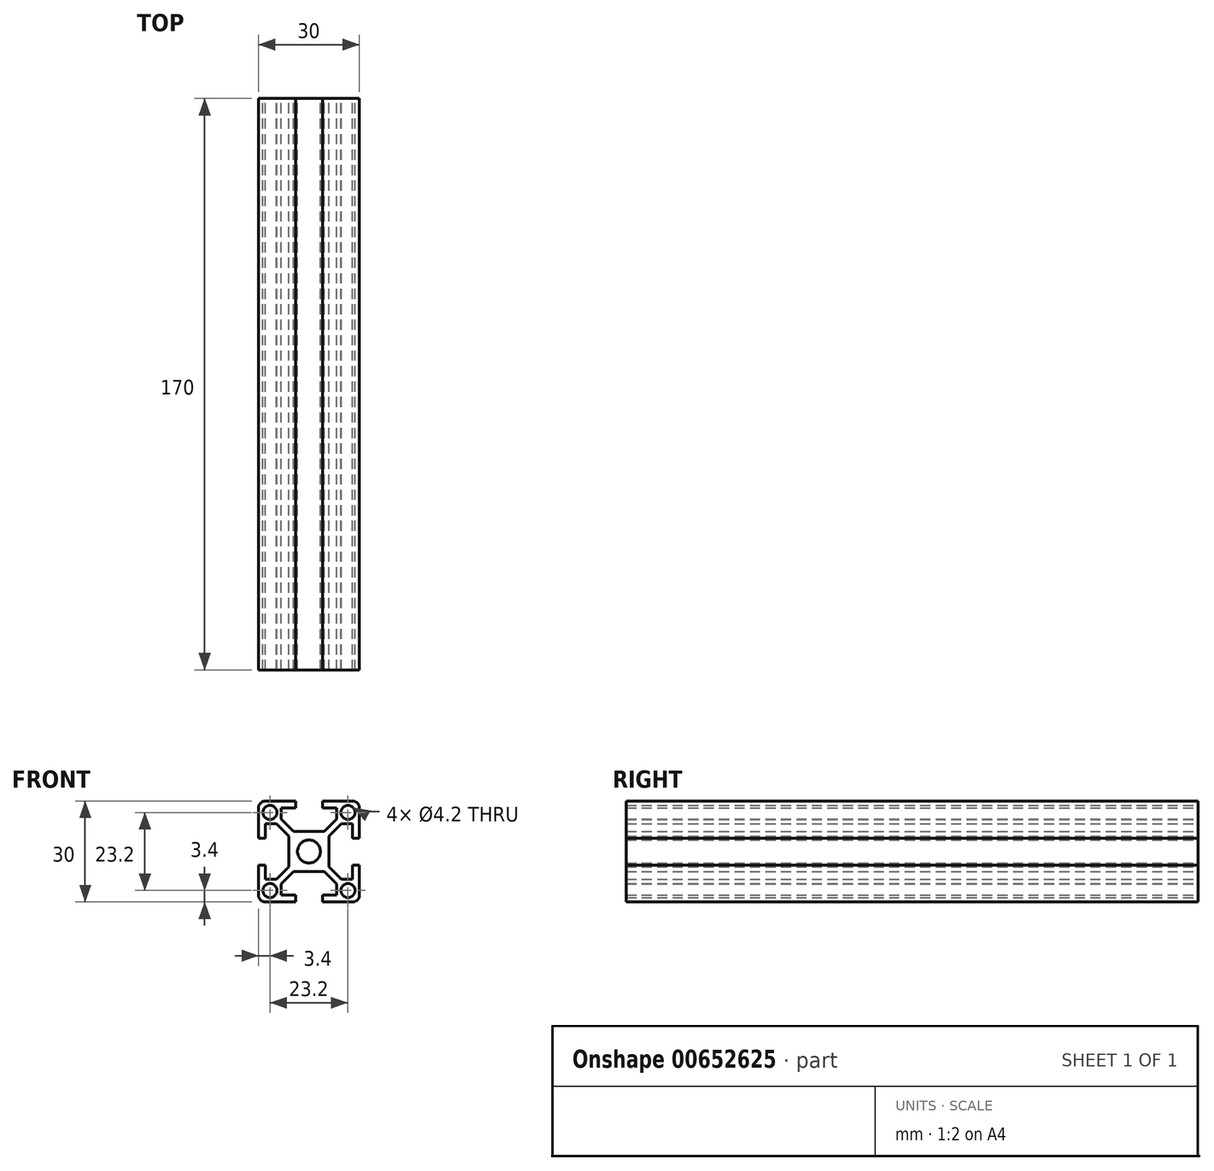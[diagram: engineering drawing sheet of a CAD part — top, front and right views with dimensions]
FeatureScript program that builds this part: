
annotation { "Feature Type Name" : "Feature", "Feature Type Description" : "" }
export const myFeature = defineFeature(function(context is Context, id is Id, definition is map)
    precondition{}
    {
        {
            var Q0;
            Q0=qCreatedBy(makeId("Front.planeOp"),FACE);
            var sketch = newSketch(context, id + "F0", { "sketchPlane" : qUnion([Q0])});
            skLineSegment(sketch, "E0", {"start": v(0, 6) * mm, "end": v(-4.59, 6) * mm});
            skLineSegment(sketch, "E1", {"start": v(-4.59, 6) * mm, "end": v(-8.25, 9.66) * mm});
            skLineSegment(sketch, "E2", {"start": v(-8.25, 9.66) * mm, "end": v(-8.25, 13) * mm});
            skLineSegment(sketch, "E3", {"start": v(-8.25, 13) * mm, "end": v(-4, 13) * mm});
            skLineSegment(sketch, "E4", {"start": v(-4, 13) * mm, "end": v(-4, 15) * mm});
            skLineSegment(sketch, "E5", {"start": v(-4, 15) * mm, "end": v(-13, 15) * mm});
            skLineSegment(sketch, "E6", {"start": v(-15, 13) * mm, "end": v(-15, 4) * mm});
            skLineSegment(sketch, "E7", {"start": v(-15, 4) * mm, "end": v(-13, 4) * mm});
            skLineSegment(sketch, "E8", {"start": v(-13, 4) * mm, "end": v(-13, 8.25) * mm});
            skLineSegment(sketch, "E9", {"start": v(-13, 8.25) * mm, "end": v(-9.66, 8.25) * mm});
            skLineSegment(sketch, "E10", {"start": v(-9.66, 8.25) * mm, "end": v(-6, 4.59) * mm});
            skLineSegment(sketch, "E11", {"start": v(-6, 4.59) * mm, "end": v(-6, 0) * mm});
            skLineSegment(sketch, "E12", {"start": v(-6, 0) * mm, "end": v(0, 0) * mm, "construction": true});
            skLineSegment(sketch, "E13", {"start": v(0, 0) * mm, "end": v(0, 6) * mm, "construction": true});
            skArc(sketch, "E14", {"start": v(0, 3.4) * mm, "mid": v(-2.4, 2.4) * mm, "end": v(-3.4, 0) * mm});
            skCircle(sketch, "E15", {"center": v(-11.6, 11.6) * mm, "radius": 2.1 * mm});
            skLineSegment(sketch, "E16", {"start": v(0, 0) * mm, "end": v(-7.38, 7.38) * mm, "construction": true});
            skLineSegment(sketch, "E17.1.0", {"start": v(-8.25, -13) * mm, "end": v(-8.25, -9.66) * mm});
            skLineSegment(sketch, "E17.1.1", {"start": v(-4, -15) * mm, "end": v(-4, -13) * mm});
            skLineSegment(sketch, "E17.1.2", {"start": v(-4, -13) * mm, "end": v(-8.25, -13) * mm});
            skLineSegment(sketch, "E17.1.3", {"start": v(-15, -4) * mm, "end": v(-15, -13) * mm});
            skLineSegment(sketch, "E17.1.4", {"start": v(-8.25, -9.66) * mm, "end": v(-4.59, -6) * mm});
            skLineSegment(sketch, "E17.1.5", {"start": v(-13, -15) * mm, "end": v(-4, -15) * mm});
            skLineSegment(sketch, "E17.1.6", {"start": v(-4.59, -6) * mm, "end": v(0, -6) * mm});
            skLineSegment(sketch, "E17.1.7", {"start": v(0, -6) * mm, "end": v(0, 0) * mm, "construction": true});
            skLineSegment(sketch, "E17.1.8", {"start": v(0, 0) * mm, "end": v(-6, 0) * mm, "construction": true});
            skLineSegment(sketch, "E17.1.9", {"start": v(-13, -4) * mm, "end": v(-15, -4) * mm});
            skLineSegment(sketch, "E17.1.10", {"start": v(-13, -8.25) * mm, "end": v(-13, -4) * mm});
            skArc(sketch, "E17.1.11", {"start": v(-3.4, 0) * mm, "mid": v(-2.4, -2.4) * mm, "end": v(0, -3.4) * mm});
            skLineSegment(sketch, "E17.1.12", {"start": v(-9.66, -8.25) * mm, "end": v(-13, -8.25) * mm});
            skLineSegment(sketch, "E17.1.13", {"start": v(0, 0) * mm, "end": v(-7.38, -7.38) * mm, "construction": true});
            skLineSegment(sketch, "E17.1.14", {"start": v(-6, -4.59) * mm, "end": v(-9.66, -8.25) * mm});
            skCircle(sketch, "E17.1.15", {"center": v(-11.6, -11.6) * mm, "radius": 2.1 * mm});
            skLineSegment(sketch, "E17.1.16", {"start": v(-6, 0) * mm, "end": v(-6, -4.59) * mm});
            skLineSegment(sketch, "E17.2.0", {"start": v(13, -8.25) * mm, "end": v(9.66, -8.25) * mm});
            skLineSegment(sketch, "E17.2.1", {"start": v(15, -4) * mm, "end": v(13, -4) * mm});
            skLineSegment(sketch, "E17.2.2", {"start": v(13, -4) * mm, "end": v(13, -8.25) * mm});
            skLineSegment(sketch, "E17.2.3", {"start": v(4, -15) * mm, "end": v(13, -15) * mm});
            skLineSegment(sketch, "E17.2.4", {"start": v(9.66, -8.25) * mm, "end": v(6, -4.59) * mm});
            skLineSegment(sketch, "E17.2.5", {"start": v(15, -13) * mm, "end": v(15, -4) * mm});
            skLineSegment(sketch, "E17.2.6", {"start": v(6, -4.59) * mm, "end": v(6, 0) * mm});
            skLineSegment(sketch, "E17.2.7", {"start": v(6, 0) * mm, "end": v(0, 0) * mm, "construction": true});
            skLineSegment(sketch, "E17.2.8", {"start": v(0, 0) * mm, "end": v(0, -6) * mm, "construction": true});
            skLineSegment(sketch, "E17.2.9", {"start": v(4, -13) * mm, "end": v(4, -15) * mm});
            skLineSegment(sketch, "E17.2.10", {"start": v(8.25, -13) * mm, "end": v(4, -13) * mm});
            skArc(sketch, "E17.2.11", {"start": v(0, -3.4) * mm, "mid": v(2.4, -2.4) * mm, "end": v(3.4, 0) * mm});
            skLineSegment(sketch, "E17.2.12", {"start": v(8.25, -9.66) * mm, "end": v(8.25, -13) * mm});
            skLineSegment(sketch, "E17.2.13", {"start": v(0, 0) * mm, "end": v(7.38, -7.38) * mm, "construction": true});
            skLineSegment(sketch, "E17.2.14", {"start": v(4.59, -6) * mm, "end": v(8.25, -9.66) * mm});
            skCircle(sketch, "E17.2.15", {"center": v(11.6, -11.6) * mm, "radius": 2.1 * mm});
            skLineSegment(sketch, "E17.2.16", {"start": v(0, -6) * mm, "end": v(4.59, -6) * mm});
            skLineSegment(sketch, "E17.3.0", {"start": v(8.25, 13) * mm, "end": v(8.25, 9.66) * mm});
            skLineSegment(sketch, "E17.3.1", {"start": v(4, 15) * mm, "end": v(4, 13) * mm});
            skLineSegment(sketch, "E17.3.2", {"start": v(4, 13) * mm, "end": v(8.25, 13) * mm});
            skLineSegment(sketch, "E17.3.3", {"start": v(15, 4) * mm, "end": v(15, 13) * mm});
            skLineSegment(sketch, "E17.3.4", {"start": v(8.25, 9.66) * mm, "end": v(4.59, 6) * mm});
            skLineSegment(sketch, "E17.3.5", {"start": v(13, 15) * mm, "end": v(4, 15) * mm});
            skLineSegment(sketch, "E17.3.6", {"start": v(4.59, 6) * mm, "end": v(0, 6) * mm});
            skLineSegment(sketch, "E17.3.7", {"start": v(0, 6) * mm, "end": v(0, 0) * mm, "construction": true});
            skLineSegment(sketch, "E17.3.8", {"start": v(0, 0) * mm, "end": v(6, 0) * mm, "construction": true});
            skLineSegment(sketch, "E17.3.9", {"start": v(13, 4) * mm, "end": v(15, 4) * mm});
            skLineSegment(sketch, "E17.3.10", {"start": v(13, 8.25) * mm, "end": v(13, 4) * mm});
            skArc(sketch, "E17.3.11", {"start": v(3.4, 0) * mm, "mid": v(2.4, 2.4) * mm, "end": v(0, 3.4) * mm});
            skLineSegment(sketch, "E17.3.12", {"start": v(9.66, 8.25) * mm, "end": v(13, 8.25) * mm});
            skLineSegment(sketch, "E17.3.13", {"start": v(0, 0) * mm, "end": v(7.38, 7.38) * mm, "construction": true});
            skLineSegment(sketch, "E17.3.14", {"start": v(6, 4.59) * mm, "end": v(9.66, 8.25) * mm});
            skCircle(sketch, "E17.3.15", {"center": v(11.6, 11.6) * mm, "radius": 2.1 * mm});
            skLineSegment(sketch, "E17.3.16", {"start": v(6, 0) * mm, "end": v(6, 4.59) * mm});
            skPoint(sketch, "E18.visualSharp", {"position": v(-15, 15) * mm});
            skArc(sketch, "E18.filletArc", {"start": v(-13, 15) * mm, "mid": v(-14.41, 14.41) * mm, "end": v(-15, 13) * mm});
            skPoint(sketch, "E19.visualSharp", {"position": v(15, 15) * mm});
            skArc(sketch, "E19.filletArc", {"start": v(15, 13) * mm, "mid": v(14.41, 14.41) * mm, "end": v(13, 15) * mm});
            skPoint(sketch, "E20.visualSharp", {"position": v(15, -15) * mm});
            skArc(sketch, "E20.filletArc", {"start": v(13, -15) * mm, "mid": v(14.41, -14.41) * mm, "end": v(15, -13) * mm});
            skPoint(sketch, "E21.visualSharp", {"position": v(-15, -15) * mm});
            skArc(sketch, "E21.filletArc", {"start": v(-15, -13) * mm, "mid": v(-14.41, -14.41) * mm, "end": v(-13, -15) * mm});
            skSolve(sketch);
        }
        {
            var Q0;
            Q0 = qSketchRegion(id + "F0", true);
            extrude(context, id + "F1", {"entities" : qUnion([Q0]), "depth" : 170 * mm, "offsetDistance" : 25 * mm});
        }
    });
